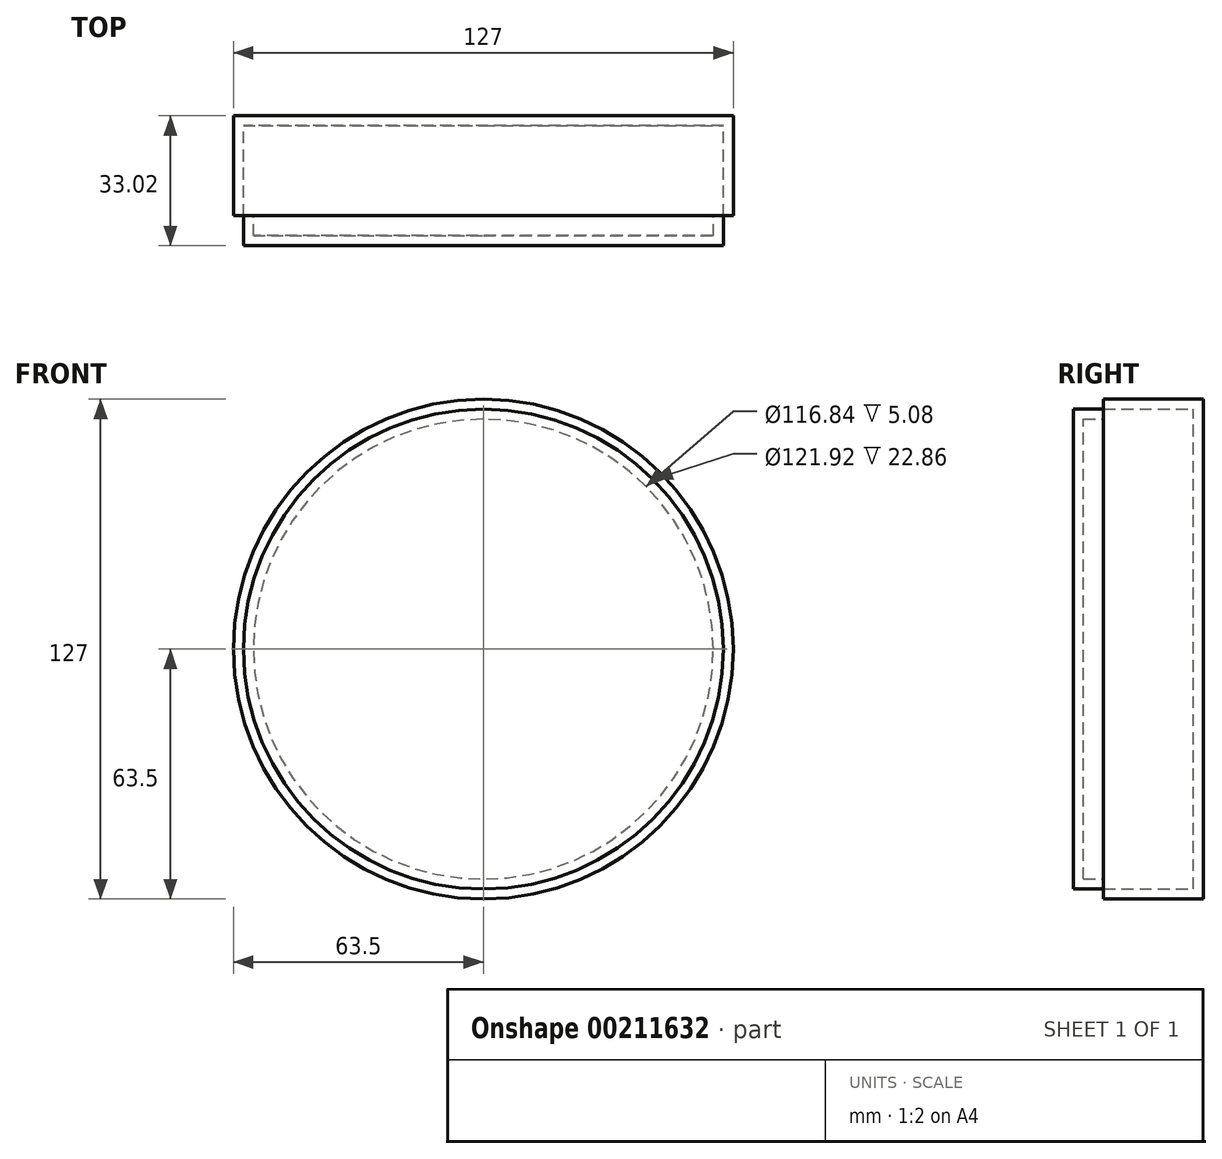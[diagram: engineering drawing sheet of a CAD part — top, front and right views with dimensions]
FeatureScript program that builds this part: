
annotation { "Feature Type Name" : "Feature", "Feature Type Description" : "" }
export const myFeature = defineFeature(function(context is Context, id is Id, definition is map)
    precondition{}
    {
        {
            var Q0;
            Q0=qCreatedBy(makeId("Front.planeOp"),FACE);
            var sketch = newSketch(context, id + "F0", { "sketchPlane" : qUnion([Q0])});
            skCircle(sketch, "E0", {"center": v(0, 0) * mm, "radius": 63.5 * mm});
            skSolve(sketch);
        }
        {
            var Q0;
            Q0=makeQuery(id+"F0.imprint","IMPRINT",FACE,{"disambiguationData":[TD([[makeQuery(id+"F0.imprint","IMPRINT",EDGE,{"derivedFrom":sQuery(id+"F0.wireOp",EDGE,"E0")}),1.0]])]});
            extrude(context, id + "F1", {"entities" : qUnion([Q0]), "depth" : 25.4 * mm});
        }
        {
            var Q0;
            Q0=makeQuery(id+"F1.opExtrude","CAP_FACE",FACE,{"disambiguationData":[OSD([sQuery(id+"F0.wireOp",EDGE,"E0")])],"isStart":false});
            shell(context, id + "F2", {"entities" : qUnion([Q0]), "thickness" : 2.54 * mm});
        }
        {
            var Q0;
            Q0=makeQuery(id+"F1.opExtrude","CAP_FACE",FACE,{"disambiguationData":[OSD([sQuery(id+"F0.wireOp",EDGE,"E0")])],"isStart":false});
            var sketch = newSketch(context, id + "F4", { "sketchPlane" : qUnion([Q0])});
            skSolve(sketch);
        }
        {
            var Q0;
            Q0 = qSketchRegion(id + "F4", true);
            var Q1;
            {var subQ0=sQuery(id+"F0.wireOp",EDGE,"E0");Q1=makeQuery(id+"F4.imprint","IMPRINT",FACE,{"disambiguationData":[TD([[makeQuery(id+"F4.imprint","IMPRINT",EDGE,{"derivedFrom":makeQuery(id+"F2.opShell","OFFSET_EDGE",EDGE,{"disambiguationData":[OSD([subQ0]),TDD([makeQuery(id+"F1.opExtrude","CAP_EDGE",EDGE,{"disambiguationData":[OSD([subQ0])],"isStart":false})])]})}),1.0]])]});}
            extrude(context, id + "F3", {"entities" : qUnion([Q0, Q1]), "depth" : 7.62 * mm});
        }
        {
            var Q0;
            Q0=makeQuery(id+"F3.opExtrude","CAP_FACE",FACE,{"disambiguationData":[OSD([sQuery(id+"F0.wireOp",EDGE,"E0")])],"isStart":true});
            shell(context, id + "F5", {"entities" : qUnion([Q0]), "thickness" : 2.54 * mm});
        }
    });
